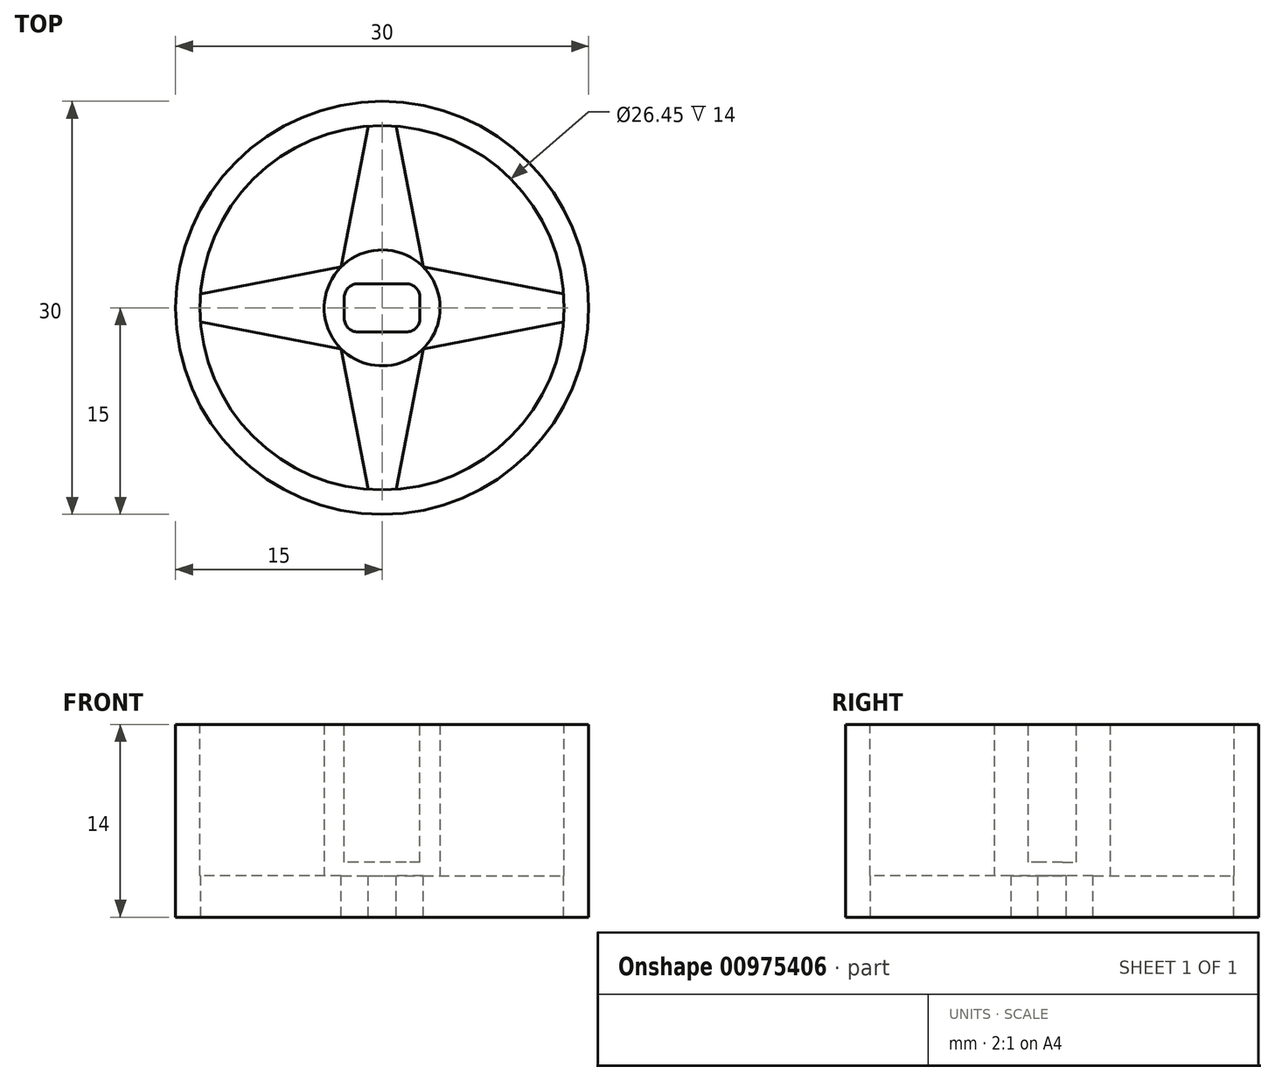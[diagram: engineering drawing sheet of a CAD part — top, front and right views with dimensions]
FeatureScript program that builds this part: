
annotation { "Feature Type Name" : "Feature", "Feature Type Description" : "" }
export const myFeature = defineFeature(function(context is Context, id is Id, definition is map)
    precondition{}
    {
        {
            var Q0;
            Q0=qCreatedBy(makeId("Top.planeOp"),FACE);
            var sketch = newSketch(context, id + "F0", { "sketchPlane" : qUnion([Q0])});
            skCircle(sketch, "E0", {"center": v(0, 0) * mm, "radius": 15 * mm});
            skSolve(sketch);
        }
        {
            var Q0;
            Q0=makeQuery(id+"F0.imprint","IMPRINT",FACE,{"disambiguationData":[TD([[makeQuery(id+"F0.imprint","IMPRINT",EDGE,{"derivedFrom":sQuery(id+"F0.wireOp",EDGE,"E0")}),1.0]])]});
            extrude(context, id + "F1", {"entities" : qUnion([Q0]), "depth" : 14 * mm, "offsetDistance" : 25 * mm});
        }
        {
            var Q0;
            Q0=makeQuery(id+"F1.opExtrude","CAP_FACE",FACE,{"disambiguationData":[OSD([sQuery(id+"F0.wireOp",EDGE,"E0")])],"isStart":false});
            var sketch = newSketch(context, id + "F2", { "sketchPlane" : qUnion([Q0])});
            skCircle(sketch, "E1", {"center": v(0, 0) * mm, "radius": 13.23 * mm});
            skSolve(sketch);
        }
        {
            var Q0;
            Q0=makeQuery(id+"F2.imprint","IMPRINT",FACE,{"disambiguationData":[TD([[makeQuery(id+"F2.imprint","IMPRINT",EDGE,{"derivedFrom":sQuery(id+"F2.wireOp",EDGE,"E1")}),1.0]])]});
            extrude(context, id + "F3", {"entities" : qUnion([Q0]), "operationType" : NewBodyOperationType.REMOVE, "oppositeDirection" : true, "depth" : 11 * mm, "offsetDistance" : 25 * mm});
        }
        {
            var Q0;
            Q0=makeQuery(id+"F3.boolean.opBoolean","COPY",FACE,{"derivedFrom":makeQuery(id+"F3.opExtrude","CAP_FACE",FACE,{"disambiguationData":[OSD([sQuery(id+"F2.wireOp",EDGE,"E1")])],"isStart":false})});
            var sketch = newSketch(context, id + "F4", { "sketchPlane" : qUnion([Q0])});
            skCircle(sketch, "E2", {"center": v(0, 0) * mm, "radius": 4.2 * mm});
            skSolve(sketch);
        }
        {
            var Q0;
            Q0=makeQuery(id+"F4.imprint","IMPRINT",FACE,{"disambiguationData":[TD([[makeQuery(id+"F4.imprint","IMPRINT",EDGE,{"derivedFrom":sQuery(id+"F4.wireOp",EDGE,"E2")}),1.0]])]});
            extrude(context, id + "F5", {"entities" : qUnion([Q0]), "operationType" : NewBodyOperationType.ADD, "depth" : 11 * mm, "offsetDistance" : 25 * mm});
        }
        {
            var Q0;
            Q0=makeQuery(id+"F3.boolean.opBoolean","COPY",FACE,{"derivedFrom":makeQuery(id+"F3.opExtrude","CAP_FACE",FACE,{"disambiguationData":[OSD([sQuery(id+"F2.wireOp",EDGE,"E1")])],"isStart":false})});
            var sketch = newSketch(context, id + "F6", { "sketchPlane" : qUnion([Q0])});
            skLineSegment(sketch, "E3", {"start": v(2.98, 2.98) * mm, "end": v(1.03, 13.19) * mm});
            skLineSegment(sketch, "E4.MirrorCS", {"start": v(-2.98, 2.98) * mm, "end": v(-1.03, 13.19) * mm});
            skLineSegment(sketch, "E5.MirrorCS", {"start": v(2.98, -2.98) * mm, "end": v(1.03, -13.19) * mm});
            skLineSegment(sketch, "E6.MirrorCS", {"start": v(-2.98, -2.98) * mm, "end": v(-1.03, -13.19) * mm});
            skLineSegment(sketch, "E7.MirrorCS", {"start": v(2.98, 2.98) * mm, "end": v(13.19, 1.03) * mm});
            skLineSegment(sketch, "E8.MirrorCS", {"start": v(2.98, -2.98) * mm, "end": v(13.19, -1.03) * mm});
            skLineSegment(sketch, "E9.MirrorCS", {"start": v(-2.98, -2.98) * mm, "end": v(-13.19, -1.03) * mm});
            skLineSegment(sketch, "E10.MirrorCS", {"start": v(-2.98, 2.98) * mm, "end": v(-13.19, 1.03) * mm});
            skArc(sketch, "E11", {"start": v(-13.19, 1.03) * mm, "mid": v(-9.35, 9.35) * mm, "end": v(-1.03, 13.19) * mm});
            skArc(sketch, "E12", {"start": v(1.03, 13.19) * mm, "mid": v(9.35, 9.35) * mm, "end": v(13.19, 1.03) * mm});
            skArc(sketch, "E13", {"start": v(13.19, -1.03) * mm, "mid": v(9.35, -9.35) * mm, "end": v(1.03, -13.19) * mm});
            skArc(sketch, "E14", {"start": v(-1.03, -13.19) * mm, "mid": v(-9.35, -9.35) * mm, "end": v(-13.19, -1.03) * mm});
            skSolve(sketch);
        }
        {
            var Q0;
            Q0=qSketchRegion(id+"F6",true);
            extrude(context, id + "F7", {"entities" : qUnion([Q0]), "operationType" : NewBodyOperationType.REMOVE, "endBound" : BoundingType.UP_TO_NEXT, "oppositeDirection" : true, "depth" : 25 * mm, "offsetDistance" : 25 * mm});
        }
        {
            var Q0;
            Q0=makeQuery(id+"F5.opExtrude","CAP_FACE",FACE,{"disambiguationData":[OSD([sQuery(id+"F4.wireOp",EDGE,"E2")])],"isStart":false});
            var sketch = newSketch(context, id + "F8", { "sketchPlane" : qUnion([Q0])});
            skLineSegment(sketch, "E15.bottom", {"start": v(2.75, 1.75) * mm, "end": v(-2.75, 1.75) * mm});
            skLineSegment(sketch, "E15.top", {"start": v(2.75, -1.75) * mm, "end": v(-2.75, -1.75) * mm});
            skPoint(sketch, "E15.middle", {"position": v(0, 0) * mm});
            skLineSegment(sketch, "E16", {"start": v(2.75, 1.75) * mm, "end": v(2.75, 0) * mm});
            skLineSegment(sketch, "E17", {"start": v(2.75, 0) * mm, "end": v(2.75, -1.75) * mm});
            skLineSegment(sketch, "E18", {"start": v(-2.75, -1.75) * mm, "end": v(-2.75, 0) * mm});
            skLineSegment(sketch, "E19", {"start": v(-2.75, 0) * mm, "end": v(-2.75, 1.75) * mm});
            skSolve(sketch);
        }
        {
            var Q0;
            Q0=makeQuery(id+"F8.imprint","IMPRINT",FACE,{"disambiguationData":[TD([[makeQuery(id+"F8.imprint","IMPRINT",EDGE,{"derivedFrom":sQuery(id+"F8.wireOp",EDGE,"E15.bottom")}),1.0]])]});
            extrude(context, id + "F9", {"entities" : qUnion([Q0]), "operationType" : NewBodyOperationType.REMOVE, "oppositeDirection" : true, "depth" : 10 * mm, "offsetDistance" : 25 * mm});
        }
        {
            var Q0;
            Q0=makeQuery(id+"F9.boolean.opBoolean","COPY",EDGE,{"derivedFrom":makeQuery(id+"F9.opExtrude","SWEPT_EDGE",EDGE,{"disambiguationData":[OSD([sQuery(id+"F8.wireOp",EDGE,"E15.bottom"),sQuery(id+"F8.wireOp",EDGE,"E19")])]})});
            var Q1;
            Q1=makeQuery(id+"F9.boolean.opBoolean","COPY",EDGE,{"derivedFrom":makeQuery(id+"F9.opExtrude","SWEPT_EDGE",EDGE,{"disambiguationData":[OSD([sQuery(id+"F8.wireOp",EDGE,"E15.top"),sQuery(id+"F8.wireOp",EDGE,"E18")])]})});
            var Q2;
            Q2=makeQuery(id+"F9.boolean.opBoolean","COPY",EDGE,{"derivedFrom":makeQuery(id+"F9.opExtrude","SWEPT_EDGE",EDGE,{"disambiguationData":[OSD([sQuery(id+"F8.wireOp",EDGE,"E15.top"),sQuery(id+"F8.wireOp",EDGE,"E17")])]})});
            var Q3;
            Q3=makeQuery(id+"F9.boolean.opBoolean","COPY",EDGE,{"derivedFrom":makeQuery(id+"F9.opExtrude","SWEPT_EDGE",EDGE,{"disambiguationData":[OSD([sQuery(id+"F8.wireOp",EDGE,"E15.bottom"),sQuery(id+"F8.wireOp",EDGE,"E16")])]})});
            fillet(context, id + "F10", {"entities" : qUnion([Q0, Q1, Q2, Q3]), "radius" : 1 * mm, "tangentPropagation" : true, "allowEdgeOverflow" : false});
        }
    });
